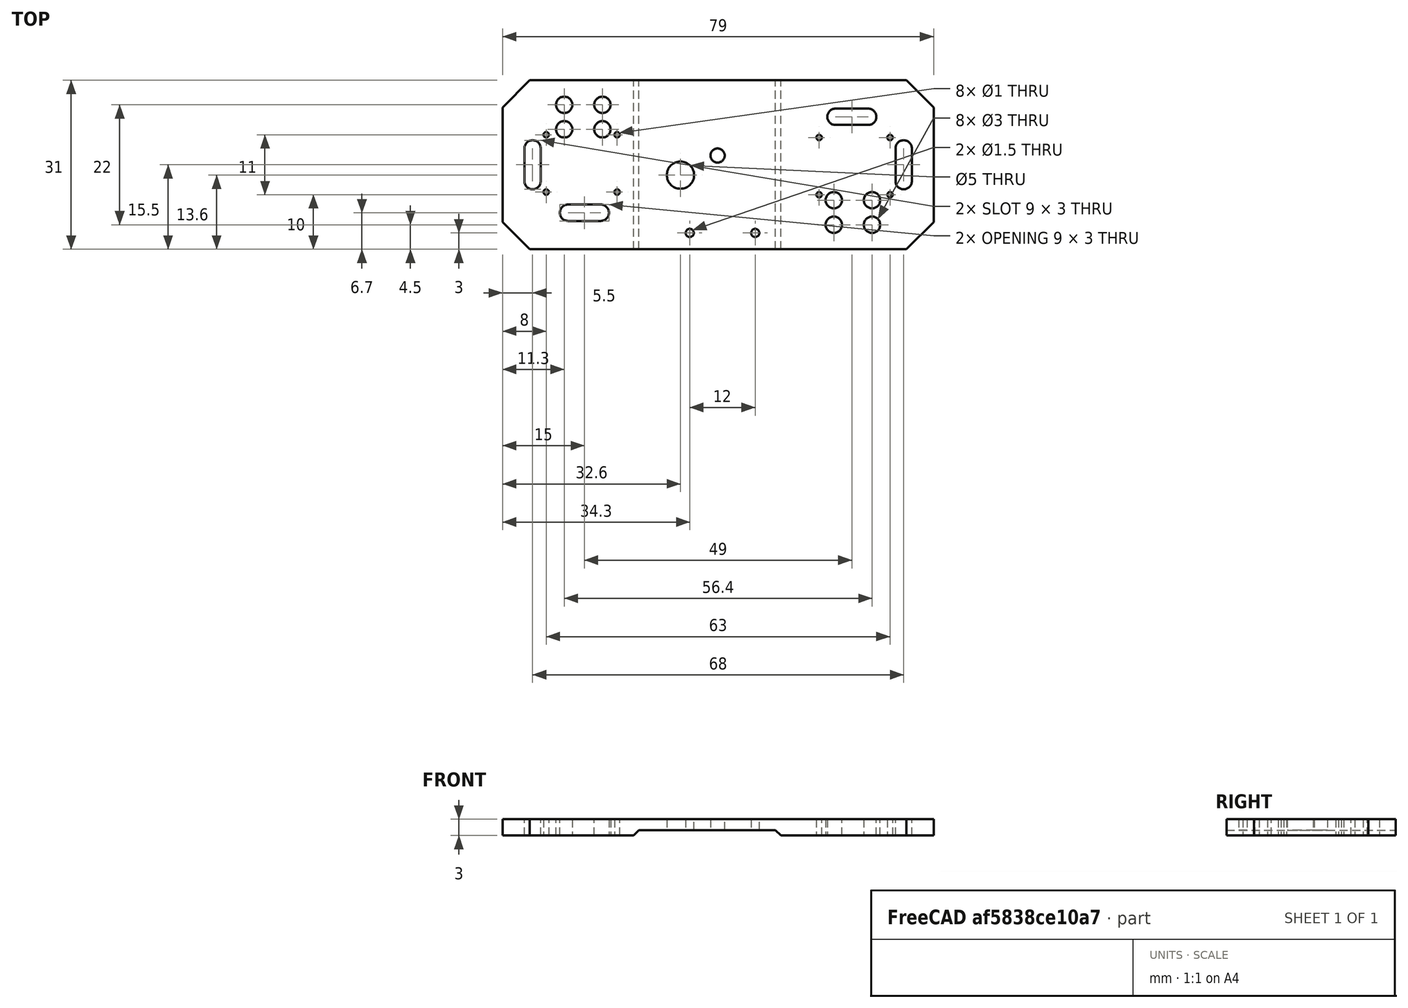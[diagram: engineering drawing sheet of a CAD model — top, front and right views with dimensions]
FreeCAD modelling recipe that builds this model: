
FCSTD DOCUMENT  (FreeCAD 0.20R26651 (Git))
Label: tx_mounting_plate
License: All rights reserved
LicenseURL: http://en.wikipedia.org/wiki/All_rights_reserved
objects: Part::Cylinder×28, Part::MultiFuse×14, Part::Box×7, Part::Cut×5, Image::ImagePlane×3, Part::Chamfer×3
note: 57 computed .brp shape members not serialized (recipe doc carries the construction recipe); baked Part::Feature solids carry a one-line shape summary decoded from their .brp

FEATURE [Image::ImagePlane] ImagePlane
  Placement = pos=(0,0,-0.01) rot=(0,0,1;1.57952rad)
  XSize = 142.095
  YSize = 252.614
FEATURE [Image::ImagePlane] ImagePlane001
  Placement = pos=(15.7,-16.3,0) rot=(0,0,1;1.5708rad)
  XSize = 28.5746
  YSize = 18.6082
FEATURE [Image::ImagePlane] ImagePlane002
  Placement = pos=(-35,-18.7,0) rot=(0,0,1;4.72984rad)
  XSize = 28.5746
  YSize = 18.6082
FEATURE [Part::Box] Box  label="Würfel"
  AttacherType = Attacher::AttachEngine3D
  Height = 2
  Length = 27
  Placement = pos=(-25,-33,1) rot=(0,0,1;0rad)
  Width = 31
FEATURE [Part::Cylinder] Cylinder  label="Zylinder"
  Angle = 360
  AttacherType = Attacher::AttachEngine3D
  FirstAngle = 0
  Height = 10
  Placement = pos=(-16.4,-19.4,0) rot=(0,0,1;0rad)
  Radius = 2.5
  SecondAngle = 0
FEATURE [Part::Cylinder] Cylinder001  label="Zylinder001"
  Angle = 360
  AttacherType = Attacher::AttachEngine3D
  FirstAngle = 0
  Height = 10
  Placement = pos=(-9.6,-15.8,0) rot=(0,0,1;0rad)
  Radius = 1.3
  SecondAngle = 0
FEATURE [Part::Cut] Cut
  Base = -> Box
  Tool = -> Cylinder
FEATURE [Part::Cut] Cut001
  Base = -> Cut
  Tool = -> Cylinder001
FEATURE [Part::Cylinder] Cylinder002  label="Zylinder002"
  Angle = 360
  AttacherType = Attacher::AttachEngine3D
  FirstAngle = 0
  Height = 10
  Placement = pos=(-2.7,-30,0) rot=(0,0,1;0rad)
  Radius = 0.75
  SecondAngle = 0
FEATURE [Part::Cylinder] Cylinder003  label="Zylinder003"
  Angle = 360
  AttacherType = Attacher::AttachEngine3D
  FirstAngle = 0
  Height = 10
  Placement = pos=(-14.7,-30,0) rot=(0,0,1;0rad)
  Radius = 0.75
  SecondAngle = 0
FEATURE [Part::MultiFuse] Fusion
  Shapes = -> [Cylinder002,Cylinder003]
FEATURE [Part::Cut] Cut002
  Base = -> Cut001
  Tool = -> Fusion
FEATURE [Part::Cylinder] Cylinder004  label="Zylinder004"
  Angle = 360
  AttacherType = Attacher::AttachEngine3D
  FirstAngle = 0
  Height = 10
  Placement = pos=(12,-8.7,0) rot=(0,0,1;0rad)
  Radius = 1.5
  SecondAngle = 0
FEATURE [Part::Cylinder] Cylinder005  label="Zylinder005"
  Angle = 360
  AttacherType = Attacher::AttachEngine3D
  FirstAngle = 0
  Height = 10
  Placement = pos=(18,-8.7,0) rot=(0,0,1;0rad)
  Radius = 1.5
  SecondAngle = 0
FEATURE [Part::Box] Box001  label="Würfel001"
  AttacherType = Attacher::AttachEngine3D
  Height = 10
  Length = 6
  Placement = pos=(12,-10.2,0) rot=(0,0,1;0rad)
  Width = 3
FEATURE [Part::MultiFuse] Fusion001
  Shapes = -> [Cylinder004,Cylinder005,Box001]
FEATURE [Part::Cylinder] Cylinder006  label="Zylinder006"
  Angle = 360
  AttacherType = Attacher::AttachEngine3D
  FirstAngle = 0
  Height = 10
  Placement = pos=(11.7,-24,0) rot=(0,0,1;0rad)
  Radius = 1.5
  SecondAngle = 0
FEATURE [Part::Cylinder] Cylinder007  label="Zylinder007"
  Angle = 360
  AttacherType = Attacher::AttachEngine3D
  FirstAngle = 0
  Height = 10
  Placement = pos=(18.7,-24,0) rot=(0,0,1;0rad)
  Radius = 1.5
  SecondAngle = 0
FEATURE [Part::Cylinder] Cylinder008  label="Zylinder008"
  Angle = 360
  AttacherType = Attacher::AttachEngine3D
  FirstAngle = 0
  Height = 10
  Placement = pos=(18.7,-28.5,0) rot=(0,0,1;0rad)
  Radius = 1.5
  SecondAngle = 0
FEATURE [Part::Cylinder] Cylinder009  label="Zylinder009"
  Angle = 360
  AttacherType = Attacher::AttachEngine3D
  FirstAngle = 0
  Height = 10
  Placement = pos=(11.7,-28.5,0) rot=(0,0,1;0rad)
  Radius = 1.5
  SecondAngle = 0
FEATURE [Part::Cylinder] Cylinder010  label="Zylinder010"
  Angle = 360
  AttacherType = Attacher::AttachEngine3D
  FirstAngle = 0
  Height = 10
  Placement = pos=(24.5,-14.5,0) rot=(0,0,1;0rad)
  Radius = 1.5
  SecondAngle = 0
FEATURE [Part::MultiFuse] Fusion002
  Shapes = -> [Cylinder006,Cylinder007,Cylinder008,Cylinder009]
FEATURE [Part::Cylinder] Cylinder011  label="Zylinder011"
  Angle = 360
  AttacherType = Attacher::AttachEngine3D
  FirstAngle = 0
  Height = 10
  Placement = pos=(24.5,-20.5,0) rot=(0,0,1;0rad)
  Radius = 1.5
  SecondAngle = 0
FEATURE [Part::Box] Box002  label="Würfel002"
  AttacherType = Attacher::AttachEngine3D
  Height = 10
  Length = 3
  Placement = pos=(23,-20.5,0) rot=(0,0,1;0rad)
  Width = 6
FEATURE [Part::MultiFuse] Fusion003
  Shapes = -> [Cylinder011,Box002,Cylinder010]
FEATURE [Part::MultiFuse] Fusion004
  Shapes = -> [Fusion001,Fusion002,Fusion003]
FEATURE [Part::Box] Box003  label="Würfel003"
  AttacherType = Attacher::AttachEngine3D
  Height = 10
  Length = 6
  Placement = pos=(12,-10.2,0) rot=(0,0,1;0rad)
  Width = 3
FEATURE [Part::Cylinder] Cylinder012  label="Zylinder012"
  Angle = 360
  AttacherType = Attacher::AttachEngine3D
  FirstAngle = 0
  Height = 10
  Placement = pos=(18,-8.7,0) rot=(0,0,1;0rad)
  Radius = 1.5
  SecondAngle = 0
FEATURE [Part::Cylinder] Cylinder013  label="Zylinder013"
  Angle = 360
  AttacherType = Attacher::AttachEngine3D
  FirstAngle = 0
  Height = 10
  Placement = pos=(12,-8.7,0) rot=(0,0,1;0rad)
  Radius = 1.5
  SecondAngle = 0
FEATURE [Part::MultiFuse] Fusion005
  Shapes = -> [Cylinder013,Cylinder012,Box003]
FEATURE [Part::Cylinder] Cylinder014  label="Zylinder014"
  Angle = 360
  AttacherType = Attacher::AttachEngine3D
  FirstAngle = 0
  Height = 10
  Placement = pos=(11.7,-24,0) rot=(0,0,1;0rad)
  Radius = 1.5
  SecondAngle = 0
FEATURE [Part::Cylinder] Cylinder015  label="Zylinder015"
  Angle = 360
  AttacherType = Attacher::AttachEngine3D
  FirstAngle = 0
  Height = 10
  Placement = pos=(18.7,-28.5,0) rot=(0,0,1;0rad)
  Radius = 1.5
  SecondAngle = 0
FEATURE [Part::Cylinder] Cylinder016  label="Zylinder016"
  Angle = 360
  AttacherType = Attacher::AttachEngine3D
  FirstAngle = 0
  Height = 10
  Placement = pos=(18.7,-24,0) rot=(0,0,1;0rad)
  Radius = 1.5
  SecondAngle = 0
FEATURE [Part::Cylinder] Cylinder017  label="Zylinder017"
  Angle = 360
  AttacherType = Attacher::AttachEngine3D
  FirstAngle = 0
  Height = 10
  Placement = pos=(24.5,-14.5,0) rot=(0,0,1;0rad)
  Radius = 1.5
  SecondAngle = 0
FEATURE [Part::Cylinder] Cylinder018  label="Zylinder018"
  Angle = 360
  AttacherType = Attacher::AttachEngine3D
  FirstAngle = 0
  Height = 10
  Placement = pos=(11.7,-28.5,0) rot=(0,0,1;0rad)
  Radius = 1.5
  SecondAngle = 0
FEATURE [Part::MultiFuse] Fusion006
  Shapes = -> [Cylinder014,Cylinder016,Cylinder015,Cylinder018]
FEATURE [Part::Cylinder] Cylinder019  label="Zylinder019"
  Angle = 360
  AttacherType = Attacher::AttachEngine3D
  FirstAngle = 0
  Height = 10
  Placement = pos=(24.5,-20.5,0) rot=(0,0,1;0rad)
  Radius = 1.5
  SecondAngle = 0
FEATURE [Part::Box] Box004  label="Würfel004"
  AttacherType = Attacher::AttachEngine3D
  Height = 10
  Length = 3
  Placement = pos=(23,-20.5,0) rot=(0,0,1;0rad)
  Width = 6
FEATURE [Part::MultiFuse] Fusion007
  Shapes = -> [Cylinder019,Box004,Cylinder017]
FEATURE [Part::MultiFuse] Fusion008
  Placement = pos=(-19,-35,0) rot=(0,0,1;3.14159rad)
  Shapes = -> [Fusion005,Fusion006,Fusion007]
FEATURE [Part::Cylinder] Cylinder020  label="Zylinder020"
  Angle = 360
  AttacherType = Attacher::AttachEngine3D
  FirstAngle = 0
  Height = 10
  Placement = pos=(-41,-12,0) rot=(0,0,1;0rad)
  Radius = 0.5
  SecondAngle = 0
FEATURE [Part::Cylinder] Cylinder021  label="Zylinder021"
  Angle = 360
  AttacherType = Attacher::AttachEngine3D
  FirstAngle = 0
  Height = 10
  Placement = pos=(-41,-22.5,0) rot=(0,0,1;0rad)
  Radius = 0.5
  SecondAngle = 0
FEATURE [Part::Cylinder] Cylinder022  label="Zylinder022"
  Angle = 360
  AttacherType = Attacher::AttachEngine3D
  FirstAngle = 0
  Height = 10
  Placement = pos=(-28,-12,0) rot=(0,0,1;0rad)
  Radius = 0.5
  SecondAngle = 0
FEATURE [Part::Cylinder] Cylinder023  label="Zylinder023"
  Angle = 360
  AttacherType = Attacher::AttachEngine3D
  FirstAngle = 0
  Height = 10
  Placement = pos=(-28,-22.5,0) rot=(0,0,1;0rad)
  Radius = 0.5
  SecondAngle = 0
FEATURE [Part::MultiFuse] Fusion009
  Shapes = -> [Cylinder020,Cylinder021,Cylinder022,Cylinder023]
FEATURE [Part::Cylinder] Cylinder024  label="Zylinder024"
  Angle = 360
  AttacherType = Attacher::AttachEngine3D
  FirstAngle = 0
  Height = 10
  Placement = pos=(-41,-12,0) rot=(0,0,1;0rad)
  Radius = 0.5
  SecondAngle = 0
FEATURE [Part::Cylinder] Cylinder025  label="Zylinder025"
  Angle = 360
  AttacherType = Attacher::AttachEngine3D
  FirstAngle = 0
  Height = 10
  Placement = pos=(-41,-22.5,0) rot=(0,0,1;0rad)
  Radius = 0.5
  SecondAngle = 0
FEATURE [Part::Cylinder] Cylinder026  label="Zylinder026"
  Angle = 360
  AttacherType = Attacher::AttachEngine3D
  FirstAngle = 0
  Height = 10
  Placement = pos=(-28,-12,0) rot=(0,0,1;0rad)
  Radius = 0.5
  SecondAngle = 0
FEATURE [Part::Cylinder] Cylinder027  label="Zylinder027"
  Angle = 360
  AttacherType = Attacher::AttachEngine3D
  FirstAngle = 0
  Height = 10
  Placement = pos=(-28,-22.5,0) rot=(0,0,1;0rad)
  Radius = 0.5
  SecondAngle = 0
FEATURE [Part::MultiFuse] Fusion010
  Placement = pos=(50,-0.5,0) rot=(0,0,1;0rad)
  Shapes = -> [Cylinder024,Cylinder025,Cylinder026,Cylinder027]
FEATURE [Part::Box] Box005  label="Würfel005"
  AttacherType = Attacher::AttachEngine3D
  Height = 3
  Length = 29
  Placement = pos=(1,-33,0) rot=(0,0,1;0rad)
  Width = 31
FEATURE [Part::MultiFuse] Fusion011
  Shapes = -> [Fusion004,Fusion010]
FEATURE [Part::MultiFuse] Fusion012
  Shapes = -> [Fusion008,Fusion009]
FEATURE [Part::Box] Box006  label="Würfel006"
  AttacherType = Attacher::AttachEngine3D
  Height = 3
  Length = 25
  Placement = pos=(-49,-33,0) rot=(0,0,1;0rad)
  Width = 31
FEATURE [Part::Cut] Cut003
  Base = -> Box005
  Tool = -> Fusion011
FEATURE [Part::Cut] Cut004
  Base = -> Box006
  Tool = -> Fusion012
FEATURE [Part::MultiFuse] Fusion013
  Shapes = -> [Cut002,Cut003,Cut004]
FEATURE [Part::Chamfer] Chamfer
  Base = -> Fusion013
  Edges = 2 edges r=5: [Edge100,Edge107]
FEATURE [Part::Chamfer] Chamfer001
  Base = -> Chamfer
  Edges = 2 edges r=5: [Edge109,Edge114]
FEATURE [Part::Chamfer] Chamfer002  label="plate"
  Base = -> Chamfer001
  Edges = 2 edges r=0.99: [Edge34,Edge101]
